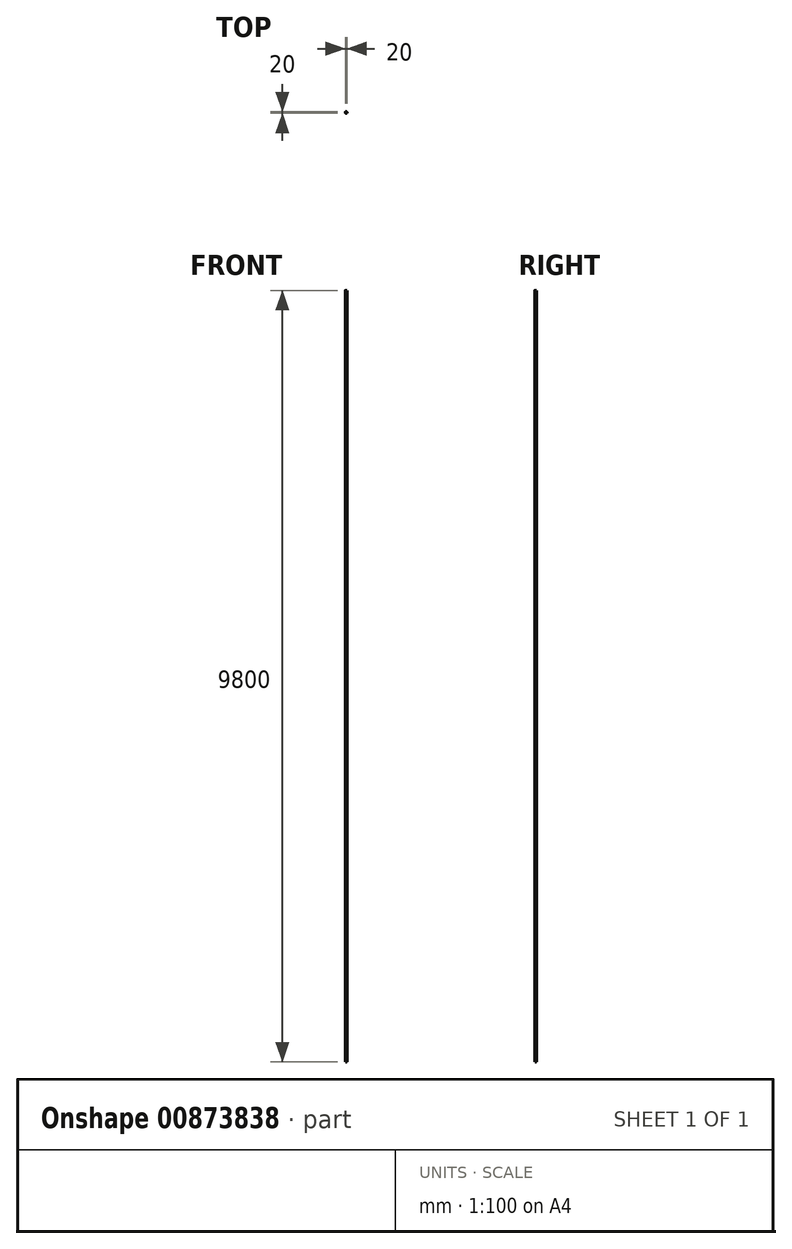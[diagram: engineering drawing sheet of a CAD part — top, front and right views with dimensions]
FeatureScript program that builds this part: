
annotation { "Feature Type Name" : "Feature", "Feature Type Description" : "" }
export const myFeature = defineFeature(function(context is Context, id is Id, definition is map)
    precondition{}
    {
        {
            var Q0;
            Q0=qCreatedBy(makeId("Top.planeOp"),FACE);
            var sketch = newSketch(context, id + "F0", { "sketchPlane" : qUnion([Q0])});
            skCircle(sketch, "E0", {"center": v(0, 0) * mm, "radius": 10 * mm});
            skSolve(sketch);
        }
        {
            var Q0;
            Q0 = qSketchRegion(id + "F0", true);
            extrude(context, id + "F1", {"entities" : qUnion([Q0]), "depth" : 9800 * mm, "offsetDistance" : 25 * mm});
        }
    });
